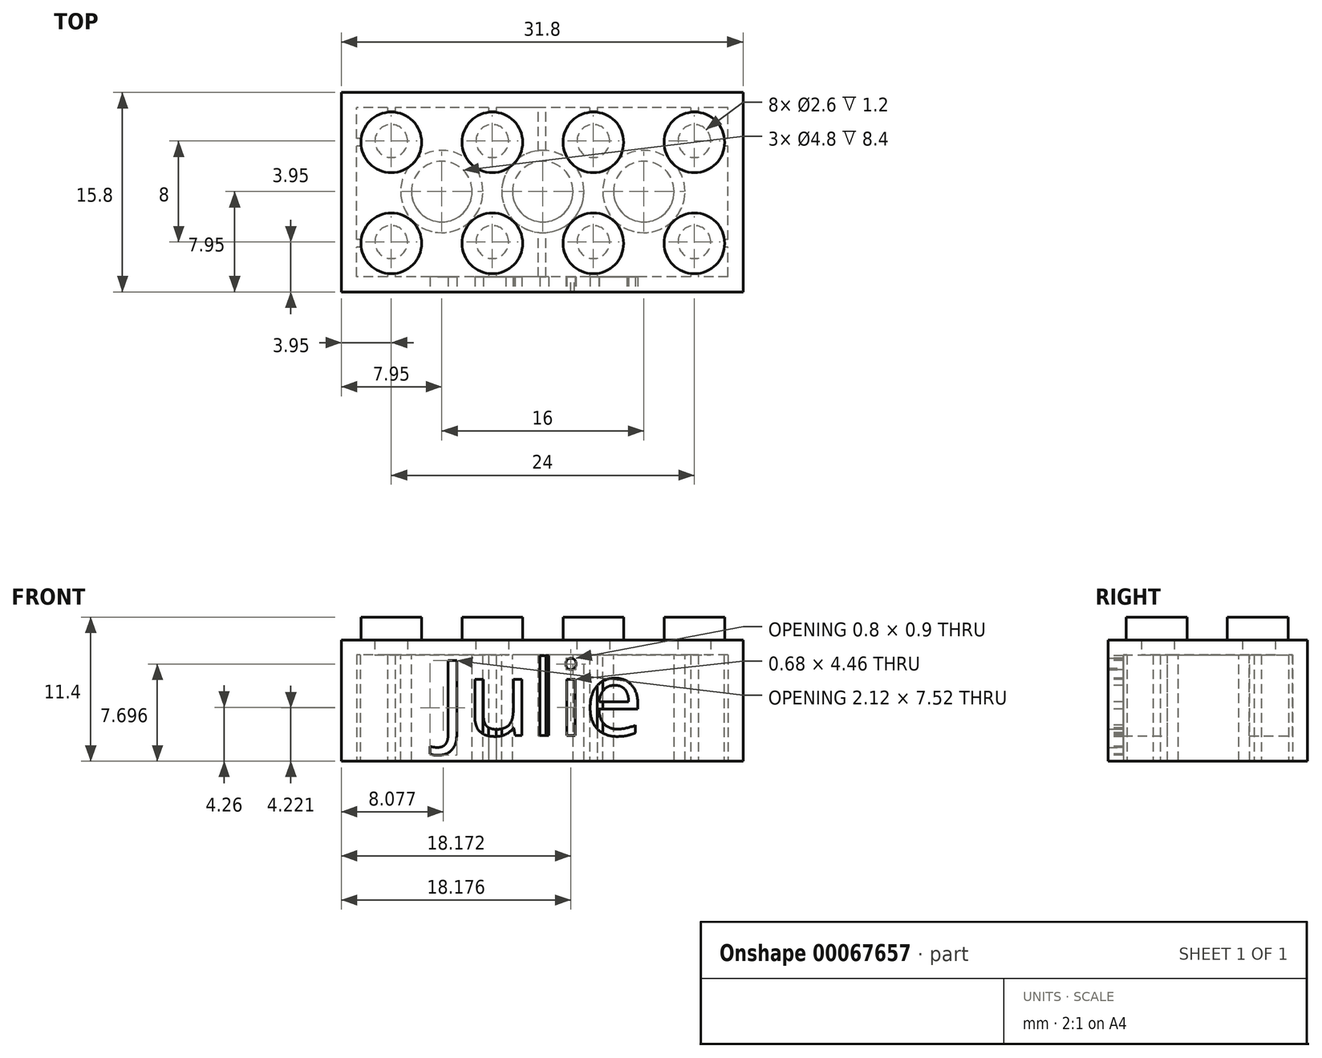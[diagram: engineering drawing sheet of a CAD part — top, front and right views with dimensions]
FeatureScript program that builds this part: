
annotation { "Feature Type Name" : "Feature", "Feature Type Description" : "" }
export const myFeature = defineFeature(function(context is Context, id is Id, definition is map)
    precondition{}
    {
        {
            var Q0;
            Q0=qCreatedBy(makeId("Top.planeOp"),FACE);
            var sketch = newSketch(context, id + "F0", { "sketchPlane" : qUnion([Q0])});
            skLineSegment(sketch, "E0.rect.bottom", {"start": v(15.9, 7.9) * mm, "end": v(-15.9, 7.9) * mm});
            skLineSegment(sketch, "E0.rect.top", {"start": v(15.9, -7.9) * mm, "end": v(-15.9, -7.9) * mm});
            skLineSegment(sketch, "E0.rect.left", {"start": v(15.9, 7.9) * mm, "end": v(15.9, -7.9) * mm});
            skLineSegment(sketch, "E0.rect.right", {"start": v(-15.9, 7.9) * mm, "end": v(-15.9, -7.9) * mm});
            skPoint(sketch, "E0.rect.middle", {"position": v(0, 0) * mm});
            skSolve(sketch);
        }
        {
            var Q0;
            Q0 = qSketchRegion(id + "F0", true);
            extrude(context, id + "F1", {"entities" : qUnion([Q0]), "depth" : 9.6 * mm});
        }
        {
            var Q0;
            Q0=makeQuery(id+"F1.opExtrude","CAP_FACE",FACE,{"disambiguationData":[OSD([sQuery(id+"F0.wireOp",EDGE,"E0.rect.bottom"),sQuery(id+"F0.wireOp",EDGE,"E0.rect.top"),sQuery(id+"F0.wireOp",EDGE,"E0.rect.left"),sQuery(id+"F0.wireOp",EDGE,"E0.rect.right")])],"isStart":true});
            var sketch = newSketch(context, id + "F2", { "sketchPlane" : qUnion([Q0])});
            skLineSegment(sketch, "E1.rect.bottom", {"start": v(14.7, 6.7) * mm, "end": v(-14.7, 6.7) * mm});
            skLineSegment(sketch, "E1.rect.top", {"start": v(14.7, -6.7) * mm, "end": v(-14.7, -6.7) * mm});
            skLineSegment(sketch, "E1.rect.left", {"start": v(14.7, 6.7) * mm, "end": v(14.7, -6.7) * mm});
            skLineSegment(sketch, "E1.rect.right", {"start": v(-14.7, 6.7) * mm, "end": v(-14.7, -6.7) * mm});
            skPoint(sketch, "E1.rect.middle", {"position": v(0, 0) * mm});
            skSolve(sketch);
        }
        {
            var Q0;
            Q0=makeQuery(id+"F2.imprint","IMPRINT",FACE,{"disambiguationData":[TD([[makeQuery(id+"F2.imprint","IMPRINT",EDGE,{"derivedFrom":sQuery(id+"F2.wireOp",EDGE,"E1.rect.bottom")}),1.0]])]});
            extrude(context, id + "F3", {"entities" : qUnion([Q0]), "operationType" : NewBodyOperationType.REMOVE, "oppositeDirection" : true, "depth" : 8.4 * mm});
        }
        {
            var Q0;
            Q0=makeQuery(id+"F1.opExtrude","CAP_FACE",FACE,{"disambiguationData":[OSD([sQuery(id+"F0.wireOp",EDGE,"E0.rect.bottom"),sQuery(id+"F0.wireOp",EDGE,"E0.rect.top"),sQuery(id+"F0.wireOp",EDGE,"E0.rect.left"),sQuery(id+"F0.wireOp",EDGE,"E0.rect.right")])],"isStart":false});
            var sketch = newSketch(context, id + "F4", { "sketchPlane" : qUnion([Q0])});
            skCircle(sketch, "E2", {"center": v(-11.95, 3.95) * mm, "radius": 2.4 * mm});
            skCircle(sketch, "E3.0.1.0", {"center": v(-11.95, -4.05) * mm, "radius": 2.4 * mm});
            skCircle(sketch, "E3.1.0.0", {"center": v(-3.95, 3.95) * mm, "radius": 2.4 * mm});
            skCircle(sketch, "E3.1.1.0", {"center": v(-3.95, -4.05) * mm, "radius": 2.4 * mm});
            skCircle(sketch, "E3.2.0.0", {"center": v(4.05, 3.95) * mm, "radius": 2.4 * mm});
            skCircle(sketch, "E3.2.1.0", {"center": v(4.05, -4.05) * mm, "radius": 2.4 * mm});
            skCircle(sketch, "E3.3.0.0", {"center": v(12.05, 3.95) * mm, "radius": 2.4 * mm});
            skCircle(sketch, "E3.3.1.0", {"center": v(12.05, -4.05) * mm, "radius": 2.4 * mm});
            skLineSegment(sketch, "E3.direction1", {"start": v(-11.95, 3.95) * mm, "end": v(-3.95, 3.95) * mm, "construction": true});
            skLineSegment(sketch, "E3.direction2", {"start": v(-11.95, 3.95) * mm, "end": v(-11.95, -4.05) * mm, "construction": true});
            skSolve(sketch);
        }
        {
            var Q0;
            Q0=makeQuery(id+"F4.imprint","IMPRINT",FACE,{"disambiguationData":[TD([[makeQuery(id+"F4.imprint","IMPRINT",EDGE,{"derivedFrom":sQuery(id+"F4.wireOp",EDGE,"E2")}),1.0]])]});
            var Q1;
            Q1=makeQuery(id+"F4.imprint","IMPRINT",FACE,{"disambiguationData":[TD([[makeQuery(id+"F4.imprint","IMPRINT",EDGE,{"derivedFrom":sQuery(id+"F4.wireOp",EDGE,"E3.1.0.0")}),1.0]])]});
            var Q2;
            Q2=makeQuery(id+"F4.imprint","IMPRINT",FACE,{"disambiguationData":[TD([[makeQuery(id+"F4.imprint","IMPRINT",EDGE,{"derivedFrom":sQuery(id+"F4.wireOp",EDGE,"E3.2.0.0")}),1.0]])]});
            var Q3;
            Q3=makeQuery(id+"F4.imprint","IMPRINT",FACE,{"disambiguationData":[TD([[makeQuery(id+"F4.imprint","IMPRINT",EDGE,{"derivedFrom":sQuery(id+"F4.wireOp",EDGE,"E3.3.0.0")}),1.0]])]});
            var Q4;
            Q4=makeQuery(id+"F4.imprint","IMPRINT",FACE,{"disambiguationData":[TD([[makeQuery(id+"F4.imprint","IMPRINT",EDGE,{"derivedFrom":sQuery(id+"F4.wireOp",EDGE,"E3.0.1.0")}),1.0]])]});
            var Q5;
            Q5=makeQuery(id+"F4.imprint","IMPRINT",FACE,{"disambiguationData":[TD([[makeQuery(id+"F4.imprint","IMPRINT",EDGE,{"derivedFrom":sQuery(id+"F4.wireOp",EDGE,"E3.1.1.0")}),1.0]])]});
            var Q6;
            Q6=makeQuery(id+"F4.imprint","IMPRINT",FACE,{"disambiguationData":[TD([[makeQuery(id+"F4.imprint","IMPRINT",EDGE,{"derivedFrom":sQuery(id+"F4.wireOp",EDGE,"E3.2.1.0")}),1.0]])]});
            var Q7;
            Q7=makeQuery(id+"F4.imprint","IMPRINT",FACE,{"disambiguationData":[TD([[makeQuery(id+"F4.imprint","IMPRINT",EDGE,{"derivedFrom":sQuery(id+"F4.wireOp",EDGE,"E3.3.1.0")}),1.0]])]});
            extrude(context, id + "F5", {"entities" : qUnion([Q0, Q1, Q2, Q3, Q4, Q5, Q6, Q7]), "operationType" : NewBodyOperationType.ADD, "depth" : 1.8 * mm});
        }
        {
            var Q0;
            Q0=makeQuery(id+"F3.boolean.opBoolean","COPY",FACE,{"derivedFrom":makeQuery(id+"F3.opExtrude","CAP_FACE",FACE,{"disambiguationData":[OSD([sQuery(id+"F2.wireOp",EDGE,"E1.rect.bottom"),sQuery(id+"F2.wireOp",EDGE,"E1.rect.top"),sQuery(id+"F2.wireOp",EDGE,"E1.rect.left"),sQuery(id+"F2.wireOp",EDGE,"E1.rect.right")])],"isStart":false})});
            var sketch = newSketch(context, id + "F6", { "sketchPlane" : qUnion([Q0])});
            skCircle(sketch, "E4", {"center": v(-11.95, 3.95) * mm, "radius": 1.3 * mm});
            skCircle(sketch, "E5.0.1.0", {"center": v(-11.95, -4.05) * mm, "radius": 1.3 * mm});
            skCircle(sketch, "E5.1.0.0", {"center": v(-3.95, 3.95) * mm, "radius": 1.3 * mm});
            skCircle(sketch, "E5.1.1.0", {"center": v(-3.95, -4.05) * mm, "radius": 1.3 * mm});
            skCircle(sketch, "E5.2.0.0", {"center": v(4.05, 3.95) * mm, "radius": 1.3 * mm});
            skCircle(sketch, "E5.2.1.0", {"center": v(4.05, -4.05) * mm, "radius": 1.3 * mm});
            skCircle(sketch, "E5.3.0.0", {"center": v(12.05, 3.95) * mm, "radius": 1.3 * mm});
            skCircle(sketch, "E5.3.1.0", {"center": v(12.05, -4.05) * mm, "radius": 1.3 * mm});
            skLineSegment(sketch, "E5.direction1", {"start": v(-11.95, 3.95) * mm, "end": v(-3.95, 3.95) * mm, "construction": true});
            skLineSegment(sketch, "E5.direction2", {"start": v(-11.95, 3.95) * mm, "end": v(-11.95, -4.05) * mm, "construction": true});
            skSolve(sketch);
        }
        {
            var Q0;
            Q0=makeQuery(id+"F6.imprint","IMPRINT",FACE,{"disambiguationData":[TD([[makeQuery(id+"F6.imprint","IMPRINT",EDGE,{"derivedFrom":sQuery(id+"F6.wireOp",EDGE,"E4")}),1.0]])]});
            var Q1;
            Q1=makeQuery(id+"F6.imprint","IMPRINT",FACE,{"disambiguationData":[TD([[makeQuery(id+"F6.imprint","IMPRINT",EDGE,{"derivedFrom":sQuery(id+"F6.wireOp",EDGE,"E5.0.1.0")}),1.0]])]});
            var Q2;
            Q2=makeQuery(id+"F6.imprint","IMPRINT",FACE,{"disambiguationData":[TD([[makeQuery(id+"F6.imprint","IMPRINT",EDGE,{"derivedFrom":sQuery(id+"F6.wireOp",EDGE,"E5.1.0.0")}),1.0]])]});
            var Q3;
            Q3=makeQuery(id+"F6.imprint","IMPRINT",FACE,{"disambiguationData":[TD([[makeQuery(id+"F6.imprint","IMPRINT",EDGE,{"derivedFrom":sQuery(id+"F6.wireOp",EDGE,"E5.1.1.0")}),1.0]])]});
            var Q4;
            Q4=makeQuery(id+"F6.imprint","IMPRINT",FACE,{"disambiguationData":[TD([[makeQuery(id+"F6.imprint","IMPRINT",EDGE,{"derivedFrom":sQuery(id+"F6.wireOp",EDGE,"E5.2.0.0")}),1.0]])]});
            var Q5;
            Q5=makeQuery(id+"F6.imprint","IMPRINT",FACE,{"disambiguationData":[TD([[makeQuery(id+"F6.imprint","IMPRINT",EDGE,{"derivedFrom":sQuery(id+"F6.wireOp",EDGE,"E5.2.1.0")}),1.0]])]});
            var Q6;
            Q6=makeQuery(id+"F6.imprint","IMPRINT",FACE,{"disambiguationData":[TD([[makeQuery(id+"F6.imprint","IMPRINT",EDGE,{"derivedFrom":sQuery(id+"F6.wireOp",EDGE,"E5.3.0.0")}),1.0]])]});
            var Q7;
            Q7=makeQuery(id+"F6.imprint","IMPRINT",FACE,{"disambiguationData":[TD([[makeQuery(id+"F6.imprint","IMPRINT",EDGE,{"derivedFrom":sQuery(id+"F6.wireOp",EDGE,"E5.3.1.0")}),1.0]])]});
            extrude(context, id + "F7", {"entities" : qUnion([Q0, Q1, Q2, Q3, Q4, Q5, Q6, Q7]), "operationType" : NewBodyOperationType.REMOVE, "oppositeDirection" : true, "depth" : 1.2 * mm});
        }
        {
            var Q0;
            Q0=makeQuery(id+"F3.boolean.opBoolean","COPY",FACE,{"derivedFrom":makeQuery(id+"F3.opExtrude","CAP_FACE",FACE,{"disambiguationData":[OSD([sQuery(id+"F2.wireOp",EDGE,"E1.rect.bottom"),sQuery(id+"F2.wireOp",EDGE,"E1.rect.top"),sQuery(id+"F2.wireOp",EDGE,"E1.rect.left"),sQuery(id+"F2.wireOp",EDGE,"E1.rect.right")])],"isStart":false})});
            var sketch = newSketch(context, id + "F8", { "sketchPlane" : qUnion([Q0])});
            skLineSegment(sketch, "E6", {"start": v(-11.95, 3.95) * mm, "end": v(-3.95, -4.05) * mm, "construction": true});
            skLineSegment(sketch, "E7", {"start": v(-3.95, 3.95) * mm, "end": v(-11.95, -4.05) * mm, "construction": true});
            skLineSegment(sketch, "E8", {"start": v(-3.95, -4.05) * mm, "end": v(4.05, 3.95) * mm, "construction": true});
            skLineSegment(sketch, "E9", {"start": v(4.05, 3.95) * mm, "end": v(12.05, -4.05) * mm, "construction": true});
            skLineSegment(sketch, "E10", {"start": v(12.05, 3.95) * mm, "end": v(4.05, -4.05) * mm, "construction": true});
            skLineSegment(sketch, "E11", {"start": v(-3.95, 3.95) * mm, "end": v(4.05, -4.05) * mm, "construction": true});
            skCircle(sketch, "E12", {"center": v(-7.95, -0.05) * mm, "radius": 2.4 * mm});
            skCircle(sketch, "E13", {"center": v(-7.95, -0.05) * mm, "radius": 3.25 * mm});
            skCircle(sketch, "E14.1.0.0", {"center": v(0.05, -0.05) * mm, "radius": 3.25 * mm});
            skCircle(sketch, "E14.1.0.1", {"center": v(0.05, -0.05) * mm, "radius": 2.4 * mm});
            skCircle(sketch, "E14.2.0.0", {"center": v(8.05, -0.05) * mm, "radius": 3.25 * mm});
            skCircle(sketch, "E14.2.0.1", {"center": v(8.05, -0.05) * mm, "radius": 2.4 * mm});
            skLineSegment(sketch, "E14.direction1", {"start": v(-7.95, -0.05) * mm, "end": v(0.05, -0.05) * mm, "construction": true});
            skSolve(sketch);
        }
        {
            var Q0;
            Q0 = qSketchRegion(id + "F8", true);
            var Q1;
            Q1=makeQuery(id+"F1.opExtrude","CAP_FACE",FACE,{"disambiguationData":[OSD([sQuery(id+"F0.wireOp",EDGE,"E0.rect.bottom"),sQuery(id+"F0.wireOp",EDGE,"E0.rect.top"),sQuery(id+"F0.wireOp",EDGE,"E0.rect.left"),sQuery(id+"F0.wireOp",EDGE,"E0.rect.right")])],"isStart":true});
            extrude(context, id + "F9", {"entities" : qUnion([Q0]), "operationType" : NewBodyOperationType.ADD, "endBound" : BoundingType.UP_TO_SURFACE, "endBoundEntityFace" : qUnion([Q1]), "depth" : 25 * mm});
        }
        {
            var Q0;
            Q0=makeQuery(id+"F1.opExtrude","CAP_FACE",FACE,{"disambiguationData":[OSD([sQuery(id+"F0.wireOp",EDGE,"E0.rect.bottom"),sQuery(id+"F0.wireOp",EDGE,"E0.rect.top"),sQuery(id+"F0.wireOp",EDGE,"E0.rect.left"),sQuery(id+"F0.wireOp",EDGE,"E0.rect.right")])],"isStart":true});
            var sketch = newSketch(context, id + "F10", { "sketchPlane" : qUnion([Q0])});
            skLineSegment(sketch, "E15.bottom", {"start": v(-12.25, 6.7) * mm, "end": v(-11.65, 6.7) * mm});
            skLineSegment(sketch, "E15.top", {"start": v(-12.25, 6.4) * mm, "end": v(-11.65, 6.4) * mm});
            skLineSegment(sketch, "E15.left", {"start": v(-12.25, 6.7) * mm, "end": v(-12.25, 6.4) * mm});
            skLineSegment(sketch, "E15.right", {"start": v(-11.65, 6.7) * mm, "end": v(-11.65, 6.4) * mm});
            skLineSegment(sketch, "E16", {"start": v(-11.95, 9.1) * mm, "end": v(-11.95, -3.95) * mm, "construction": true});
            skLineSegment(sketch, "E17.0.1.0", {"start": v(-12.25, -6.7) * mm, "end": v(-11.65, -6.7) * mm});
            skLineSegment(sketch, "E17.0.1.1", {"start": v(-12.25, -6.4) * mm, "end": v(-12.25, -6.7) * mm});
            skLineSegment(sketch, "E17.0.1.2", {"start": v(-12.25, -6.4) * mm, "end": v(-11.65, -6.4) * mm});
            skLineSegment(sketch, "E17.0.1.3", {"start": v(-11.65, -6.4) * mm, "end": v(-11.65, -6.7) * mm});
            skLineSegment(sketch, "E17.1.0.0", {"start": v(-4.25, 6.4) * mm, "end": v(-3.65, 6.4) * mm});
            skLineSegment(sketch, "E17.1.0.1", {"start": v(-4.25, 6.7) * mm, "end": v(-4.25, 6.4) * mm});
            skLineSegment(sketch, "E17.1.0.2", {"start": v(-4.25, 6.7) * mm, "end": v(-3.65, 6.7) * mm});
            skLineSegment(sketch, "E17.1.0.3", {"start": v(-3.65, 6.7) * mm, "end": v(-3.65, 6.4) * mm});
            skLineSegment(sketch, "E17.1.1.0", {"start": v(-4.25, -6.7) * mm, "end": v(-3.65, -6.7) * mm});
            skLineSegment(sketch, "E17.1.1.1", {"start": v(-4.25, -6.4) * mm, "end": v(-4.25, -6.7) * mm});
            skLineSegment(sketch, "E17.1.1.2", {"start": v(-4.25, -6.4) * mm, "end": v(-3.65, -6.4) * mm});
            skLineSegment(sketch, "E17.1.1.3", {"start": v(-3.65, -6.4) * mm, "end": v(-3.65, -6.7) * mm});
            skLineSegment(sketch, "E17.2.0.0", {"start": v(3.75, 6.4) * mm, "end": v(4.35, 6.4) * mm});
            skLineSegment(sketch, "E17.2.0.1", {"start": v(3.75, 6.7) * mm, "end": v(3.75, 6.4) * mm});
            skLineSegment(sketch, "E17.2.0.2", {"start": v(3.75, 6.7) * mm, "end": v(4.35, 6.7) * mm});
            skLineSegment(sketch, "E17.2.0.3", {"start": v(4.35, 6.7) * mm, "end": v(4.35, 6.4) * mm});
            skLineSegment(sketch, "E17.2.1.0", {"start": v(3.75, -6.7) * mm, "end": v(4.35, -6.7) * mm});
            skLineSegment(sketch, "E17.2.1.1", {"start": v(3.75, -6.4) * mm, "end": v(3.75, -6.7) * mm});
            skLineSegment(sketch, "E17.2.1.2", {"start": v(3.75, -6.4) * mm, "end": v(4.35, -6.4) * mm});
            skLineSegment(sketch, "E17.2.1.3", {"start": v(4.35, -6.4) * mm, "end": v(4.35, -6.7) * mm});
            skLineSegment(sketch, "E17.3.0.0", {"start": v(11.75, 6.4) * mm, "end": v(12.35, 6.4) * mm});
            skLineSegment(sketch, "E17.3.0.1", {"start": v(11.75, 6.7) * mm, "end": v(11.75, 6.4) * mm});
            skLineSegment(sketch, "E17.3.0.2", {"start": v(11.75, 6.7) * mm, "end": v(12.35, 6.7) * mm});
            skLineSegment(sketch, "E17.3.0.3", {"start": v(12.35, 6.7) * mm, "end": v(12.35, 6.4) * mm});
            skLineSegment(sketch, "E17.3.1.0", {"start": v(11.75, -6.7) * mm, "end": v(12.35, -6.7) * mm});
            skLineSegment(sketch, "E17.3.1.1", {"start": v(11.75, -6.4) * mm, "end": v(11.75, -6.7) * mm});
            skLineSegment(sketch, "E17.3.1.2", {"start": v(11.75, -6.4) * mm, "end": v(12.35, -6.4) * mm});
            skLineSegment(sketch, "E17.3.1.3", {"start": v(12.35, -6.4) * mm, "end": v(12.35, -6.7) * mm});
            skLineSegment(sketch, "E17.direction1", {"start": v(-12.25, 6.4) * mm, "end": v(-4.25, 6.4) * mm, "construction": true});
            skLineSegment(sketch, "E17.direction2", {"start": v(-12.25, 6.4) * mm, "end": v(-12.25, -6.7) * mm, "construction": true});
            skSolve(sketch);
        }
        {
            var Q0;
            Q0 = qSketchRegion(id + "F10", true);
            var Q1;
            {var subQ0=sQuery(id+"F2.wireOp",EDGE,"E1.rect.bottom");var subQ1=sQuery(id+"F2.wireOp",EDGE,"E1.rect.top");var subQ2=sQuery(id+"F2.wireOp",EDGE,"E1.rect.left");var subQ3=sQuery(id+"F2.wireOp",EDGE,"E1.rect.right");Q1=makeQuery(id+"F9.boolean.opBoolean","SPLIT",FACE,{"disambiguationData":[TD([makeQuery(id+"F3.boolean.opBoolean","COPY",FACE,{"derivedFrom":makeQuery(id+"F3.opExtrude","SWEPT_FACE",FACE,{"disambiguationData":[OSD([subQ0])]})})])],"derivedFrom":makeQuery(id+"F3.boolean.opBoolean","COPY",FACE,{"derivedFrom":makeQuery(id+"F3.opExtrude","CAP_FACE",FACE,{"disambiguationData":[OSD([subQ0,subQ1,subQ2,subQ3])],"isStart":false})})});}
            extrude(context, id + "F11", {"entities" : qUnion([Q0]), "operationType" : NewBodyOperationType.ADD, "endBound" : BoundingType.UP_TO_SURFACE, "oppositeDirection" : true, "endBoundEntityFace" : qUnion([Q1]), "depth" : 25 * mm});
        }
        {
            var Q0;
            Q0=makeQuery(id+"F10.imprint","IMPRINT",FACE,{"disambiguationData":[TD([[makeQuery(id+"F10.imprint","IMPRINT",EDGE,{"derivedFrom":sQuery(id+"F10.wireOp",EDGE,"E15.top")}),-1.0]])]});
            var sketch = newSketch(context, id + "F12", { "sketchPlane" : qUnion([Q0])});
            skLineSegment(sketch, "E18.bottom", {"start": v(-14.7, 4.35) * mm, "end": v(-14.4, 4.35) * mm});
            skLineSegment(sketch, "E18.top", {"start": v(-14.7, 3.75) * mm, "end": v(-14.4, 3.75) * mm});
            skLineSegment(sketch, "E18.left", {"start": v(-14.7, 4.35) * mm, "end": v(-14.7, 3.75) * mm});
            skLineSegment(sketch, "E18.right", {"start": v(-14.4, 4.35) * mm, "end": v(-14.4, 3.75) * mm});
            skLineSegment(sketch, "E19", {"start": v(-31.72, 4.05) * mm, "end": v(-11.95, 4.05) * mm, "construction": true});
            skLineSegment(sketch, "E20.0.1.0", {"start": v(-14.7, -4.25) * mm, "end": v(-14.4, -4.25) * mm});
            skLineSegment(sketch, "E20.0.1.1", {"start": v(-14.7, -3.65) * mm, "end": v(-14.7, -4.25) * mm});
            skLineSegment(sketch, "E20.0.1.2", {"start": v(-14.7, -3.65) * mm, "end": v(-14.4, -3.65) * mm});
            skLineSegment(sketch, "E20.0.1.3", {"start": v(-14.4, -3.65) * mm, "end": v(-14.4, -4.25) * mm});
            skLineSegment(sketch, "E20.1.0.0", {"start": v(14.4, 3.75) * mm, "end": v(14.7, 3.75) * mm});
            skLineSegment(sketch, "E20.1.0.1", {"start": v(14.4, 4.35) * mm, "end": v(14.4, 3.75) * mm});
            skLineSegment(sketch, "E20.1.0.2", {"start": v(14.4, 4.35) * mm, "end": v(14.7, 4.35) * mm});
            skLineSegment(sketch, "E20.1.0.3", {"start": v(14.7, 4.35) * mm, "end": v(14.7, 3.75) * mm});
            skLineSegment(sketch, "E20.1.1.0", {"start": v(14.4, -4.25) * mm, "end": v(14.7, -4.25) * mm});
            skLineSegment(sketch, "E20.1.1.1", {"start": v(14.4, -3.65) * mm, "end": v(14.4, -4.25) * mm});
            skLineSegment(sketch, "E20.1.1.2", {"start": v(14.4, -3.65) * mm, "end": v(14.7, -3.65) * mm});
            skLineSegment(sketch, "E20.1.1.3", {"start": v(14.7, -3.65) * mm, "end": v(14.7, -4.25) * mm});
            skLineSegment(sketch, "E20.direction1", {"start": v(-14.7, 3.75) * mm, "end": v(14.4, 3.75) * mm, "construction": true});
            skLineSegment(sketch, "E20.direction2", {"start": v(-14.7, 3.75) * mm, "end": v(-14.7, -4.25) * mm, "construction": true});
            skSolve(sketch);
        }
        {
            var Q0;
            Q0 = qSketchRegion(id + "F12", true);
            var Q1;
            {var subQ0=sQuery(id+"F2.wireOp",EDGE,"E1.rect.bottom");var subQ1=sQuery(id+"F2.wireOp",EDGE,"E1.rect.top");var subQ2=sQuery(id+"F2.wireOp",EDGE,"E1.rect.left");var subQ3=sQuery(id+"F2.wireOp",EDGE,"E1.rect.right");Q1=makeQuery(id+"F9.boolean.opBoolean","SPLIT",FACE,{"disambiguationData":[TD([makeQuery(id+"F3.boolean.opBoolean","COPY",FACE,{"derivedFrom":makeQuery(id+"F3.opExtrude","SWEPT_FACE",FACE,{"disambiguationData":[OSD([subQ0])]})})])],"derivedFrom":makeQuery(id+"F3.boolean.opBoolean","COPY",FACE,{"derivedFrom":makeQuery(id+"F3.opExtrude","CAP_FACE",FACE,{"disambiguationData":[OSD([subQ0,subQ1,subQ2,subQ3])],"isStart":false})})});}
            extrude(context, id + "F13", {"entities" : qUnion([Q0]), "operationType" : NewBodyOperationType.ADD, "endBound" : BoundingType.UP_TO_SURFACE, "oppositeDirection" : true, "endBoundEntityFace" : qUnion([Q1]), "depth" : 25 * mm});
        }
        {
            var Q0;
            Q0=qCreatedBy(makeId("Top.planeOp"),FACE);
            cPlane(context, id + "F14", {"entities" : qUnion([Q0]), "cplaneType" : CPlaneType.OFFSET, "offset" : 8.4 * mm, "width" : 150 * mm, "height" : 150 * mm});
        }
        {
            var Q0;
            Q0=qCreatedBy(id+"F14.planeOp",FACE);
            var sketch = newSketch(context, id + "F15", { "sketchPlane" : qUnion([Q0])});
            skLineSegment(sketch, "E21.bottom", {"start": v(-0.3, -7) * mm, "end": v(0.3, -7) * mm});
            skLineSegment(sketch, "E21.top", {"start": v(-0.3, -3) * mm, "end": v(0.3, -3) * mm});
            skLineSegment(sketch, "E21.left", {"start": v(-0.3, -7) * mm, "end": v(-0.3, -3) * mm});
            skLineSegment(sketch, "E21.right", {"start": v(0.3, -7) * mm, "end": v(0.3, -3) * mm});
            skLineSegment(sketch, "E22.bottom", {"start": v(-0.3, 2.9) * mm, "end": v(0.3, 2.9) * mm});
            skLineSegment(sketch, "E22.top", {"start": v(-0.3, 6.92) * mm, "end": v(0.3, 6.92) * mm});
            skLineSegment(sketch, "E22.left", {"start": v(-0.3, 2.9) * mm, "end": v(-0.3, 6.92) * mm});
            skLineSegment(sketch, "E22.right", {"start": v(0.3, 2.9) * mm, "end": v(0.3, 6.92) * mm});
            skSolve(sketch);
        }
        {
            var Q0;
            Q0 = qSketchRegion(id + "F15", true);
            extrude(context, id + "F16", {"entities" : qUnion([Q0]), "operationType" : NewBodyOperationType.ADD, "oppositeDirection" : true, "depth" : 6.4 * mm});
        }
        {
            var Q0;
            Q0=makeQuery(id+"F1.opExtrude","SWEPT_FACE",FACE,{"disambiguationData":[OSD([sQuery(id+"F0.wireOp",EDGE,"E0.rect.top")])]});
            var sketch = newSketch(context, id + "F17", { "sketchPlane" : qUnion([Q0])});
            skText(sketch, "E23", { "text": "Julie\n", "fontName": "OpenSans-Regular.ttf"});
            const initialGuessF17  = {"E23": [-0.00823, 0.00203, 1, 0, 0.006]};
            skSetInitialGuess(sketch, initialGuessF17);
            skSolve(sketch);
        }
        {
            var Q0;
            Q0 = qSketchRegion(id + "F17", true);
            extrude(context, id + "F18", {"entities" : qUnion([Q0]), "operationType" : NewBodyOperationType.REMOVE, "oppositeDirection" : true, "depth" : 1.2 * mm});
        }
    });
